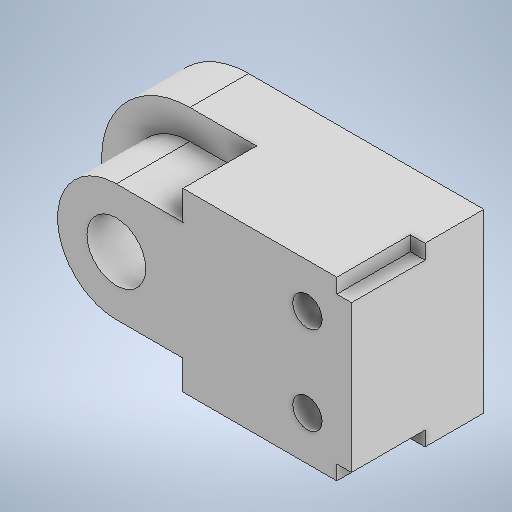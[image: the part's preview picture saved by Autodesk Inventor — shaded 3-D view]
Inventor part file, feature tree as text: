
AUTODESK INVENTOR PART (.ipt)
format: ipt  version: 2025.2 (Build 292293000, 293)  size: 320,000 bytes
history: native  units: in
note: dims shown in document units (in); Inventor stores cm internally (conversion verified against a paired STEP export)
features: sketch x4, extrude x3, emboss x1
ambient origin geometry x8: Origin, YZ Plane, XZ Plane, XY Plane, X Axis, Y Axis, Z Axis, Center Point
bodies: Solid1 (feature_tree)
feature tree (8):
  extrude  "Extrusion1"  Depth=2.3622in
  extrude  "Extrusion2"  Depth=0.7874in
  extrude  "Extrusion3"  Depth=0.1969in
  emboss  "Emboss1"
  sketch  "Sketch1"  dims[d0=3.1496in d1=2.3622in]
  sketch  "Sketch2"  dims[d2=0.7874in d3=0.0in d4=0.7874in]
  sketch  "Sketch3"  dims[d6=0.1969in d7=0.1969in d8=0.1969in]
  sketch  "Sketch4"  dims[d9=0.9843in d10=0.0in d11=0.7874in d12=0.3937in d14=0.5906in d16=0.5906in d17=0.0in d18=0.0in d19=0.0787in d20=0.0in]
